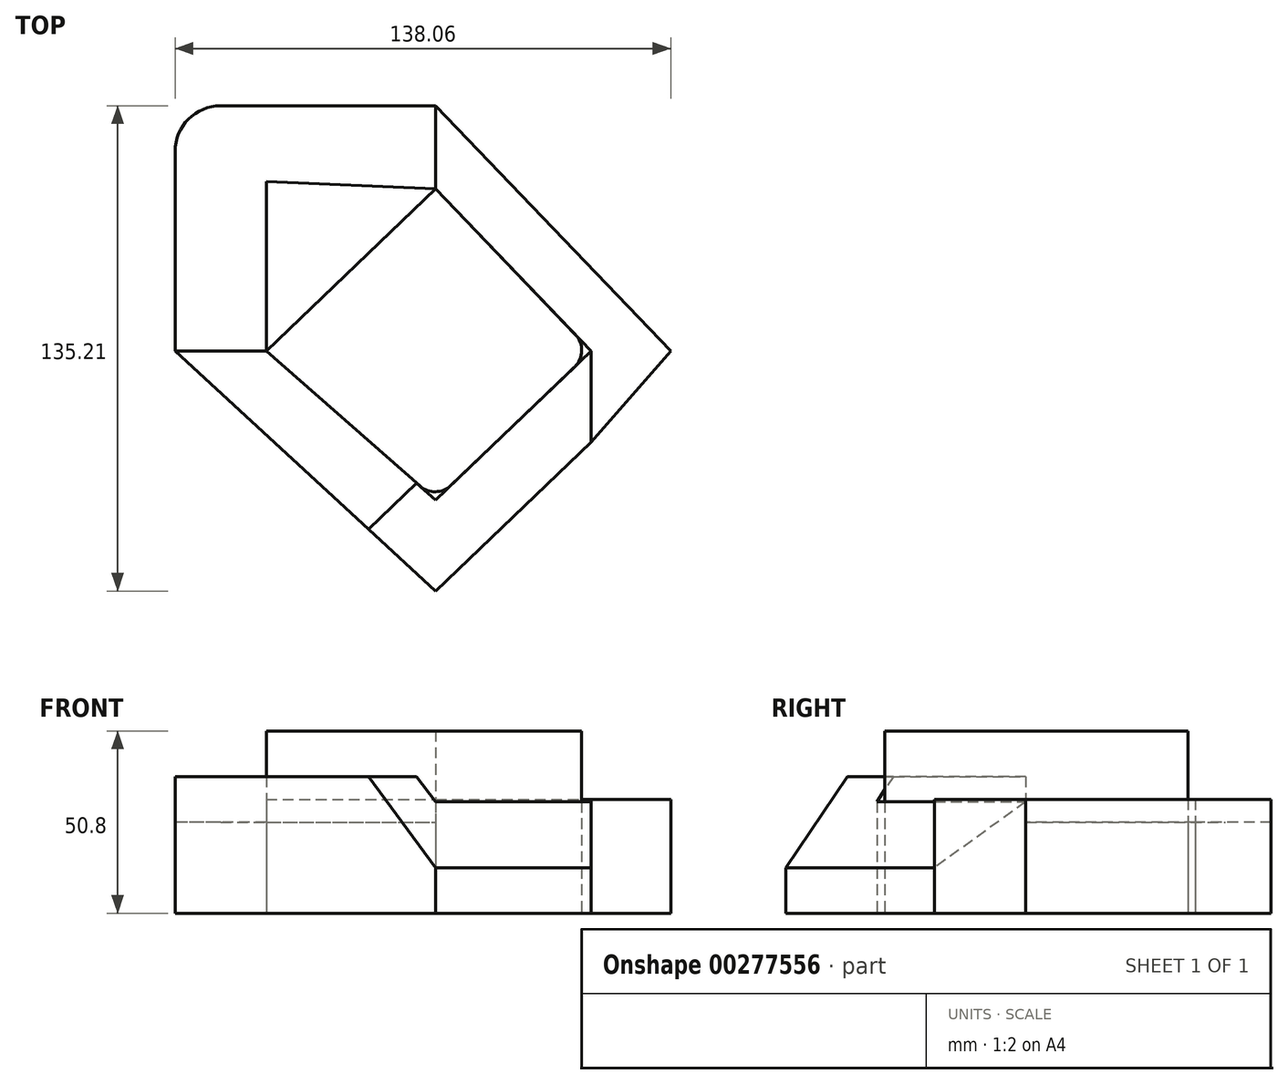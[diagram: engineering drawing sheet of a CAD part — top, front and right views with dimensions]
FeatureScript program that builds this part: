
annotation { "Feature Type Name" : "Feature", "Feature Type Description" : "" }
export const myFeature = defineFeature(function(context is Context, id is Id, definition is map)
    precondition{}
    {
        {
            var Q0;
            Q0=qCreatedBy(makeId("Top.planeOp"),FACE);
            var sketch = newSketch(context, id + "F0", { "sketchPlane" : qUnion([Q0])});
            skLineSegment(sketch, "E0", {"start": v(-47.19, 0) * mm, "end": v(0, 45.2) * mm});
            skLineSegment(sketch, "E1", {"start": v(0, 45.2) * mm, "end": v(43.29, 0) * mm});
            skLineSegment(sketch, "E2", {"start": v(43.29, 0) * mm, "end": v(0, -41.46) * mm});
            skLineSegment(sketch, "E3", {"start": v(0, -41.46) * mm, "end": v(-47.19, 0) * mm});
            skLineSegment(sketch, "E4", {"start": v(-47.19, 0) * mm, "end": v(-23.6, 22.6) * mm});
            skLineSegment(sketch, "E5", {"start": v(-23.6, 22.6) * mm, "end": v(-47.19, 47.23) * mm});
            skLineSegment(sketch, "E6", {"start": v(-47.19, 47.23) * mm, "end": v(0, 45.2) * mm});
            skLineSegment(sketch, "E7", {"start": v(-47.19, 47.23) * mm, "end": v(-47.19, 0) * mm});
            skLineSegment(sketch, "E8", {"start": v(0, -41.46) * mm, "end": v(0, -66.86) * mm});
            skLineSegment(sketch, "E9", {"start": v(43.29, 0) * mm, "end": v(43.29, -25.4) * mm});
            skLineSegment(sketch, "E10", {"start": v(0, -66.86) * mm, "end": v(43.29, -25.4) * mm});
            skLineSegment(sketch, "E11", {"start": v(-47.19, 0) * mm, "end": v(-72.59, 0) * mm});
            skLineSegment(sketch, "E12", {"start": v(-72.59, 0) * mm, "end": v(0, -66.86) * mm});
            skLineSegment(sketch, "E13", {"start": v(-72.59, 0) * mm, "end": v(-72.59, 68.35) * mm});
            skLineSegment(sketch, "E14", {"start": v(-72.59, 68.35) * mm, "end": v(0, 68.35) * mm});
            skLineSegment(sketch, "E15", {"start": v(0, 68.35) * mm, "end": v(0, 45.2) * mm});
            skLineSegment(sketch, "E16", {"start": v(0, 68.35) * mm, "end": v(65.47, 0) * mm});
            skLineSegment(sketch, "E17", {"start": v(43.29, -25.4) * mm, "end": v(65.47, 0) * mm});
            skSolve(sketch);
        }
        {
            var Q0;
            Q0=makeQuery(id+"F0.imprint","IMPRINT",FACE,{"disambiguationData":[TD([[makeQuery(id+"F0.imprint","IMPRINT",EDGE,{"derivedFrom":sQuery(id+"F0.wireOp",EDGE,"E0")}),-1.0]])]});
            extrude(context, id + "F1", {"entities" : qUnion([Q0]), "depth" : 50.8 * mm});
        }
        {
            var Q0;
            Q0=makeQuery(id+"F0.imprint","IMPRINT",FACE,{"disambiguationData":[TD([[makeQuery(id+"F0.imprint","IMPRINT",EDGE,{"derivedFrom":sQuery(id+"F0.wireOp",EDGE,"E2")}),1.0]])]});
            var Q1;
            Q1=makeQuery(id+"F0.imprint","IMPRINT",FACE,{"disambiguationData":[TD([[makeQuery(id+"F0.imprint","IMPRINT",EDGE,{"derivedFrom":sQuery(id+"F0.wireOp",EDGE,"E3")}),1.0]])]});
            extrude(context, id + "F2", {"entities" : qUnion([Q0, Q1]), "depth" : 38.1 * mm});
        }
        {
            var Q0;
            Q0=makeQuery(id+"F0.imprint","IMPRINT",FACE,{"disambiguationData":[TD([[makeQuery(id+"F0.imprint","IMPRINT",EDGE,{"derivedFrom":sQuery(id+"F0.wireOp",EDGE,"E6")}),1.0]])]});
            extrude(context, id + "F3", {"entities" : qUnion([Q0]), "depth" : 25.4 * mm});
        }
        {
            var Q0;
            Q0=makeQuery(id+"F0.imprint","IMPRINT",FACE,{"disambiguationData":[TD([[makeQuery(id+"F0.imprint","IMPRINT",EDGE,{"derivedFrom":sQuery(id+"F0.wireOp",EDGE,"E0")}),1.0]])]});
            var Q1;
            Q1=makeQuery(id+"F0.imprint","IMPRINT",FACE,{"disambiguationData":[TD([[makeQuery(id+"F0.imprint","IMPRINT",EDGE,{"derivedFrom":sQuery(id+"F0.wireOp",EDGE,"E4")}),1.0]])]});
            extrude(context, id + "F4", {"entities" : qUnion([Q0, Q1]), "depth" : 31.75 * mm});
        }
        {
            var Q0;
            Q0=makeQuery(id+"F0.imprint","IMPRINT",FACE,{"disambiguationData":[TD([[makeQuery(id+"F0.imprint","IMPRINT",EDGE,{"derivedFrom":sQuery(id+"F0.wireOp",EDGE,"E1")}),1.0]])]});
            extrude(context, id + "F5", {"entities" : qUnion([Q0]), "depth" : 31.75 * mm});
        }
        {
            var Q0;
            Q0=makeQuery(id+"F2.opExtrude","CAP_EDGE",EDGE,{"disambiguationData":[OSD([sQuery(id+"F0.wireOp",EDGE,"E10")])],"isStart":false});
            chamfer(context, id + "F6", {"entities" : qUnion([Q0]), "chamferType" : ChamferType.OFFSET_ANGLE, "width" : 25.4 * mm, "oppositeDirection" : false, "angle" : 45 * degree, "tangentPropagation" : true});
        }
        {
            var Q0;
            Q0=makeQuery(id+"F1.opExtrude","SWEPT_EDGE",EDGE,{"disambiguationData":[OSD([sQuery(id+"F0.wireOp",EDGE,"E1"),sQuery(id+"F0.wireOp",EDGE,"E2"),sQuery(id+"F0.wireOp",EDGE,"E9")])]});
            fillet(context, id + "F7", {"entities" : qUnion([Q0]), "radius" : 6.35 * mm, "tangentPropagation" : true, "allowEdgeOverflow" : false});
        }
        {
            var Q0;
            Q0=makeQuery(id+"F3.opExtrude","SWEPT_EDGE",EDGE,{"disambiguationData":[OSD([sQuery(id+"F0.wireOp",EDGE,"E13"),sQuery(id+"F0.wireOp",EDGE,"E14")])]});
            fillet(context, id + "F8", {"entities" : qUnion([Q0]), "radius" : 12.7 * mm, "tangentPropagation" : true, "allowEdgeOverflow" : false});
        }
        {
            var Q0;
            Q0=makeQuery(id+"F1.opExtrude","SWEPT_EDGE",EDGE,{"disambiguationData":[OSD([sQuery(id+"F0.wireOp",EDGE,"E2"),sQuery(id+"F0.wireOp",EDGE,"E3"),sQuery(id+"F0.wireOp",EDGE,"E8")])]});
            fillet(context, id + "F9", {"entities" : qUnion([Q0]), "radius" : 6.35 * mm, "tangentPropagation" : true, "allowEdgeOverflow" : false});
        }
    });
